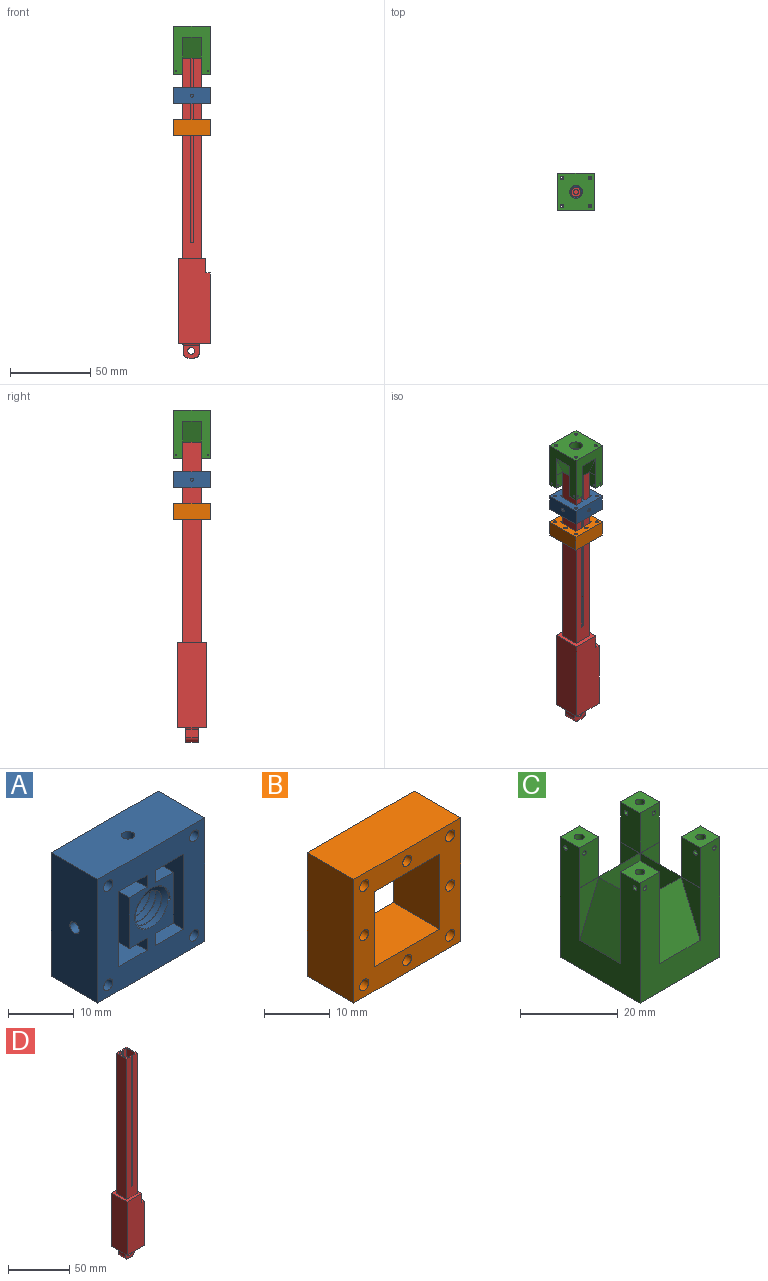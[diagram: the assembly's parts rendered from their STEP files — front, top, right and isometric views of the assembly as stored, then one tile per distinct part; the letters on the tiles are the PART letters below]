
ASSEMBLY  parts=4 mates=7
PART A: 42 faces, bbox 23.6x11.5x23.6 mm
  f0: cylinder r=1mm len=10mm, axis (0,-1,0), area 62.8mm2, adj f23,f24
  f1: cylinder r=1mm len=10mm, axis (0,-1,0), area 62.8mm2, adj f23,f24
  f2: cylinder r=1mm len=10mm, axis (0,-1,0), area 62.8mm2, adj f23,f24
  f3: cylinder r=1mm len=4mm, axis (-1,0,0), area 25.1mm2, adj f4,f32
  f4: plane 2x2mm, normal (-1,0,0), area 3.1mm2, adj f3
  f5: cylinder r=1mm len=4mm, axis (0,0,-1), area 25.1mm2, adj f6,f31
  f6: plane 2x2mm, normal (0,0,-1), area 3.1mm2, adj f5
  f7: cylinder r=1mm len=4mm, axis (1,0,0), area 25.1mm2, adj f8,f38
  f8: plane 2x2mm, normal (1,0,0), area 3.1mm2, adj f7
  f9: plane 10x2.25mm, normal (1,0,0), area 22.5mm2, adj f21,f23,f24,f35
  f10: plane 10x2.25mm, normal (-1,0,0), area 22.5mm2, adj f12,f23,f24,f29
  f11: plane 10x3.85mm, normal (0,0,-1), area 38.5mm2, adj f22,f23,f24,f28
  f12: plane 10x3.85mm, normal (0,0,1), area 38.5mm2, adj f10,f22,f23,f24
  f13: plane 0.54x0.26mm, normal (0,0,1), area 0.1mm2, adj f17,f18,f23,f26
  f14: bspline ~9.47x9.17mm, area 18.6mm2, adj f15,f18,f23,f25
  f15: bspline ~10.3x9.24mm, area 170.5mm2, adj f14,f16,f23,f25
  f16: cylinder r=3.12mm len=9.75mm, axis (0,1,0), area 16.6mm2, adj f15,f17,f23,f25
  f17: bspline ~10.51x9.25mm, area 181.5mm2, adj f13,f16,f23,f24,f25,f26
  f18: cylinder r=4.1mm len=10mm, axis (0,-1,0), area 34.7mm2, adj f13,f14,f23,f24,f25,f26
  f19: plane 10x3.85mm, normal (0,0,-1), area 38.5mm2, adj f20,f23,f24,f27
  f20: plane 10x9.5mm, normal (1,0,0), area 95mm2, adj f19,f21,f23,f24
  f21: plane 10x3.85mm, normal (0,0,1), area 38.5mm2, adj f9,f20,f23,f24
  f22: plane 10x9.5mm, normal (-1,0,0), area 95mm2, adj f11,f12,f23,f24
  f23: plane 23.59x23.59mm, normal (0,-1,0), area 376.9mm2, adj f0,f1,f2,f9,f10,f11,f12,f13
  f24: plane 23.14x23.14mm, normal (0,1,0), area 367.6mm2, adj f0,f1,f2,f9,f10,f11,f12,f17
  f25: plane 0.98x0.88mm, normal (0,0,-1), area 0.6mm2, adj f14,f15,f16,f17,f18,f24
  f26: bspline ~9.79x9.47mm, area 18.6mm2, adj f13,f17,f18,f24
  f27: plane 10x2.25mm, normal (1,0,0), area 22.5mm2, adj f19,f23,f24,f30
  f28: plane 10x2.25mm, normal (-1,0,0), area 22.5mm2, adj f11,f23,f24,f37
  f29: plane 10x6.1mm, normal (0,0,-1), area 61mm2, adj f10,f23,f24,f36
  f30: plane 10x6.1mm, normal (0,0,1), area 61mm2, adj f23,f24,f27,f34
  f31: plane 23x10mm, normal (0,0,-1), area 226.9mm2, adj f5,f23,f24,f32,f38
  f32: plane 23x10mm, normal (-1,0,0), area 226.9mm2, adj f3,f23,f24,f31,f33
  f33: plane 23x10mm, normal (0,0,1), area 226.9mm2, adj f23,f24,f32,f38,f39
  f34: plane 14x10mm, normal (-1,0,0), area 140mm2, adj f23,f24,f30,f35
  f35: plane 10x6.1mm, normal (0,0,-1), area 61mm2, adj f9,f23,f24,f34
  f36: plane 14x10mm, normal (1,0,0), area 140mm2, adj f23,f24,f29,f37
  f37: plane 10x6.1mm, normal (0,0,1), area 61mm2, adj f23,f24,f28,f36
  f38: plane 23x10mm, normal (1,0,0), area 226.9mm2, adj f7,f23,f24,f31,f33
  f39: cylinder r=1mm len=4mm, axis (0,0,1), area 25.1mm2, adj f33,f40
  f40: plane 2x2mm, normal (0,0,1), area 3.1mm2, adj f39
  f41: cylinder r=1mm len=10mm, axis (0,-1,0), area 62.8mm2, adj f23,f24
PART B: 18 faces, bbox 23x10x23 mm
  f0: cylinder r=1mm len=10mm, axis (0,-1,0), area 62.8mm2, adj f11,f12
  f1: cylinder r=1mm len=10mm, axis (0,-1,0), area 62.8mm2, adj f11,f12
  f2: cylinder r=1mm len=10mm, axis (0,-1,0), area 62.8mm2, adj f11,f12
  f3: plane 23x10mm, normal (0,0,-1), area 230mm2, adj f4,f10,f11,f12
  f4: plane 23x10mm, normal (1,0,0), area 230mm2, adj f3,f5,f11,f12
  f5: plane 23x10mm, normal (0,0,1), area 230mm2, adj f4,f10,f11,f12
  f6: plane 14x10mm, normal (-1,0,0), area 140mm2, adj f7,f9,f11,f12
  f7: plane 14x10mm, normal (0,0,1), area 140mm2, adj f6,f8,f11,f12
  f8: plane 14x10mm, normal (1,0,0), area 140mm2, adj f7,f9,f11,f12
  f9: plane 14x10mm, normal (0,0,-1), area 140mm2, adj f6,f8,f11,f12
  f10: plane 23x10mm, normal (-1,0,0), area 230mm2, adj f3,f5,f11,f12
  f11: plane 23x23mm, normal (0,-1,0), area 309.1mm2, adj f0,f1,f2,f3,f4,f5,f6,f7
  f12: plane 23x23mm, normal (0,1,0), area 309.1mm2, adj f0,f1,f2,f3,f4,f5,f6,f7
  f13: cylinder r=0.95mm len=10mm, axis (0,-1,0), area 59.7mm2, adj f11,f12
  f14: cylinder r=0.95mm len=10mm, axis (0,-1,0), area 59.7mm2, adj f11,f12
  f15: cylinder r=0.95mm len=10mm, axis (0,-1,0), area 59.7mm2, adj f11,f12
  f16: cylinder r=0.95mm len=10mm, axis (0,-1,0), area 59.7mm2, adj f11,f12
  f17: cylinder r=1mm len=10mm, axis (0,-1,0), area 62.8mm2, adj f11,f12
PART C: 63 faces, bbox 23x23x30 mm
  f0: cylinder r=4mm len=8mm, axis (0,0,-1), area 125.7mm2, adj f17,f22
  f1: cylinder r=0.5mm len=1.5mm, axis (1,0,0), area 3.7mm2, adj f13,f60,f61
  f2: plane 5.5x0.1mm, normal (0,0,1), area 0.6mm2, adj f15,f18,f54,f56
  f3: plane 5.5x0.1mm, normal (0,0,1), area 0.5mm2, adj f13,f19,f25,f57
  f4: cylinder r=0.5mm len=1.5mm, axis (0,-1,0), area 3.7mm2, adj f15,f50,f51
  f5: plane 5.5x0.1mm, normal (0,0,1), area 0.6mm2, adj f16,f21,f44,f46
  f6: plane 5.5x0.1mm, normal (0,0,1), area 0.6mm2, adj f15,f18,f47,f55
  f7: cylinder r=0.5mm len=1.5mm, axis (-1,0,0), area 3.7mm2, adj f16,f40,f41
  f8: plane 5.5x0.1mm, normal (0,0,1), area 0.6mm2, adj f10,f20,f34,f36
  f9: plane 5.5x0.1mm, normal (0,0,1), area 0.6mm2, adj f16,f21,f37,f45
  f10: plane 30x23mm, normal (0,1,0), area 415mm2, adj f8,f11,f13,f14,f16,f17,f27,f28
  f11: cylinder r=0.5mm len=1.5mm, axis (0,1,0), area 3.7mm2, adj f10,f30,f31
  f12: plane 5.5x0.1mm, normal (0,0,1), area 0.6mm2, adj f13,f19,f24,f26
  f13: plane 30x23mm, normal (1,0,0), area 415mm2, adj f1,f3,f10,f12,f15,f17,f23,f24
  f14: plane 5.5x0.1mm, normal (0,0,1), area 0.6mm2, adj f10,f20,f27,f35
  f15: plane 30x23mm, normal (0,-1,0), area 415mm2, adj f2,f4,f6,f13,f16,f17,f47,f48
  f16: plane 30x23mm, normal (-1,0,0), area 415mm2, adj f5,f7,f9,f10,f15,f17,f37,f38
  f17: plane 23x23mm, normal (0,0,-1), area 466.2mm2, adj f0,f10,f13,f15,f16,f32,f42,f52
  f18: plane 15x12mm, normal (0,1,0), area 180mm2, adj f2,f6,f19,f21,f22,f53
  f19: plane 15x12mm, normal (-1,0,0), area 180mm2, adj f3,f12,f18,f20,f22,f23
  f20: plane 15x12mm, normal (0,-1,0), area 180mm2, adj f8,f14,f19,f21,f22,f33
  f21: plane 15x12mm, normal (1,0,0), area 180mm2, adj f5,f9,f18,f20,f22,f43
  f22: plane 12x12mm, normal (0,0,1), area 93.7mm2, adj f0,f18,f19,f20,f21
  f23: plane 13x11.8mm, normal (0.92,0,0.39), area 166.6mm2, adj f13,f19,f24,f25
  f24: plane 13x5.5mm, normal (0,-1,0), area 35.8mm2, adj f12,f13,f23
  f25: plane 13x5.5mm, normal (0,1,0), area 35.8mm2, adj f3,f13,f23
  f26: plane 10x5.5mm, normal (0,-1,0), area 54.2mm2, adj f12,f13,f27,f28,f29
  f27: plane 10x5.5mm, normal (-1,0,0), area 54.2mm2, adj f10,f14,f26,f28,f31
  f28: plane 5.5x5.5mm, normal (0,0,1), area 27.1mm2, adj f10,f13,f26,f27,f32
  f29: cylinder r=0.5mm len=4mm, axis (0,1,0), area 10.5mm2, adj f26,f30,f31,f32
  f30: cylinder r=0.5mm len=1.5mm, axis (1,0,0), area 3.7mm2, adj f11,f13,f29
  f31: cylinder r=0.5mm len=4mm, axis (1,0,0), area 10.5mm2, adj f11,f27,f29,f32
  f32: cylinder r=1mm len=30mm, axis (0,0,1), area 186.5mm2, adj f17,f28,f29,f31
  f33: plane 13x11.8mm, normal (0,0.92,0.39), area 166.6mm2, adj f10,f20,f34,f35
  f34: plane 13x5.5mm, normal (1,0,0), area 35.8mm2, adj f8,f10,f33
  f35: plane 13x5.5mm, normal (-1,0,0), area 35.8mm2, adj f10,f14,f33
  f36: plane 10x5.5mm, normal (1,0,0), area 54.2mm2, adj f8,f10,f37,f38,f39
  f37: plane 10x5.5mm, normal (0,-1,0), area 54.2mm2, adj f9,f16,f36,f38,f41
  f38: plane 5.5x5.5mm, normal (0,0,1), area 27.1mm2, adj f10,f16,f36,f37,f42
  f39: cylinder r=0.5mm len=4mm, axis (-1,0,0), area 10.5mm2, adj f36,f40,f41,f42
  f40: cylinder r=0.5mm len=1.5mm, axis (0,1,0), area 3.7mm2, adj f7,f10,f39
  f41: cylinder r=0.5mm len=4mm, axis (0,1,0), area 10.5mm2, adj f7,f37,f39,f42
  f42: cylinder r=1mm len=30mm, axis (0,0,1), area 186.5mm2, adj f17,f38,f39,f41
  f43: plane 13x11.8mm, normal (-0.92,0,0.39), area 166.6mm2, adj f16,f21,f44,f45
  f44: plane 13x5.5mm, normal (0,1,0), area 35.8mm2, adj f5,f16,f43
  f45: plane 13x5.5mm, normal (0,-1,0), area 35.8mm2, adj f9,f16,f43
  f46: plane 10x5.5mm, normal (0,1,0), area 54.2mm2, adj f5,f16,f47,f48,f49
  f47: plane 10x5.5mm, normal (1,0,0), area 54.2mm2, adj f6,f15,f46,f48,f51
  f48: plane 5.5x5.5mm, normal (0,0,1), area 27.1mm2, adj f15,f16,f46,f47,f52
  f49: cylinder r=0.5mm len=4mm, axis (0,-1,0), area 10.5mm2, adj f46,f50,f51,f52
  f50: cylinder r=0.5mm len=1.5mm, axis (-1,0,0), area 3.7mm2, adj f4,f16,f49
  f51: cylinder r=0.5mm len=4mm, axis (-1,0,0), area 10.5mm2, adj f4,f47,f49,f52
  f52: cylinder r=1mm len=30mm, axis (0,0,1), area 186.5mm2, adj f17,f48,f49,f51
  f53: plane 13x11.8mm, normal (0,-0.92,0.39), area 166.6mm2, adj f15,f18,f54,f55
  f54: plane 13x5.5mm, normal (-1,0,0), area 35.8mm2, adj f2,f15,f53
  f55: plane 13x5.5mm, normal (1,0,0), area 35.8mm2, adj f6,f15,f53
  f56: plane 10x5.5mm, normal (-1,0,0), area 54.2mm2, adj f2,f15,f57,f58,f59
  f57: plane 10x5.5mm, normal (0,1,0), area 54.2mm2, adj f3,f13,f56,f58,f61
  f58: plane 5.5x5.5mm, normal (0,0,1), area 27.1mm2, adj f13,f15,f56,f57,f62
  f59: cylinder r=0.5mm len=4mm, axis (1,0,0), area 10.5mm2, adj f56,f60,f61,f62
  f60: cylinder r=0.5mm len=1.5mm, axis (0,-1,0), area 3.7mm2, adj f1,f15,f59
  f61: cylinder r=0.5mm len=4mm, axis (0,-1,0), area 10.5mm2, adj f1,f57,f59,f62
  f62: cylinder r=1mm len=30mm, axis (0,0,1), area 186.5mm2, adj f17,f58,f59,f61
PART D: 39 faces, bbox 20x18x202 mm
  f0: plane 140x12mm, normal (0,-1,0), area 1420mm2, adj f1,f3,f13,f14,f17,f34,f35,f36
  f1: plane 12x5mm, normal (0,0,1), area 20mm2, adj f0,f10,f12,f14,f15,f16,f31,f36
  f2: plane 20x18mm, normal (0,0,-1), area 240mm2, adj f4,f7,f8,f9,f27,f28,f29,f30
  f3: plane 18x17mm, normal (0,0,1), area 162mm2, adj f0,f6,f7,f8,f9,f13,f14,f15
  f4: plane 44x18mm, normal (1,0,0), area 792mm2, adj f2,f5,f8,f9
  f5: plane 18x3mm, normal (0,0,1), area 54mm2, adj f4,f6,f8,f9
  f6: plane 18x9mm, normal (1,0,0), area 162mm2, adj f3,f5,f8,f9
  f7: plane 53x18mm, normal (-1,0,0), area 954mm2, adj f2,f3,f8,f9
  f8: plane 53x20mm, normal (0,-1,0), area 1033mm2, adj f2,f3,f4,f5,f6,f7
  f9: plane 53x20mm, normal (0,1,0), area 1033mm2, adj f2,f3,f4,f5,f6,f7
  f10: plane 140x10mm, normal (0,1,0), area 1140mm2, adj f1,f11,f16,f17,f18,f34,f35,f36
  f11: plane 140x10mm, normal (1,0,0), area 1400mm2, adj f10,f12,f17,f18
  f12: plane 140x10mm, normal (0,-1,0), area 1140mm2, adj f1,f11,f16,f17,f18,f31,f32,f33
  f13: plane 140x12mm, normal (-1,0,0), area 1680mm2, adj f0,f3,f15,f17
  f14: plane 140x12mm, normal (1,0,0), area 1680mm2, adj f0,f1,f3,f15
  f15: plane 140x12mm, normal (0,1,0), area 1420mm2, adj f1,f3,f13,f14,f17,f31,f32,f33
  f16: plane 140x10mm, normal (-1,0,0), area 1400mm2, adj f1,f10,f12,f18
  f17: plane 12x5mm, normal (0,0,1), area 20mm2, adj f0,f10,f11,f12,f13,f15,f33,f34
  f18: plane 10x10mm, normal (0,0,1), area 92.9mm2, adj f10,f11,f12,f16,f37
  f19: plane 8x5mm, normal (-1,0,0), area 40mm2, adj f20,f22,f26,f27
  f20: plane 10x8mm, normal (0,1,0), area 62mm2, adj f19,f21,f23,f24,f25,f26,f28
  f21: plane 8x5mm, normal (1,0,0), area 40mm2, adj f20,f22,f25,f30
  f22: plane 10x8mm, normal (0,-1,0), area 62mm2, adj f19,f21,f23,f24,f25,f26,f29
  f23: plane 8x4mm, normal (0,0,-1), area 32mm2, adj f20,f22,f25,f26
  f24: cylinder r=2.12mm len=8mm, axis (0,-1,0), area 106.8mm2, adj f20,f22
  f25: cylinder r=3mm len=8mm, axis (0,1,0), area 37.7mm2, adj f20,f21,f22,f23
  f26: cylinder r=3mm len=8mm, axis (0,-1,0), area 37.7mm2, adj f19,f20,f22,f23
  f27: cylinder r=1mm len=10mm, axis (0,1,0), area 13.7mm2, adj f2,f19,f28,f29
  f28: cylinder r=1mm len=12mm, axis (1,0,0), area 16.8mm2, adj f2,f20,f27,f30
  f29: cylinder r=1mm len=12mm, axis (-1,0,0), area 16.8mm2, adj f2,f22,f27,f30
  f30: cylinder r=1mm len=10mm, axis (0,-1,0), area 13.7mm2, adj f2,f21,f28,f29
  f31: plane 130x1mm, normal (-1,0,0), area 130mm2, adj f1,f12,f15,f32
  f32: plane 2x1mm, normal (0,0,1), area 2mm2, adj f12,f15,f31,f33
  f33: plane 130x1mm, normal (1,0,0), area 130mm2, adj f12,f15,f17,f32
  f34: plane 130x1mm, normal (1,0,0), area 130mm2, adj f0,f10,f17,f35
  f35: plane 2x1mm, normal (0,0,1), area 2mm2, adj f0,f10,f34,f36
  f36: plane 130x1mm, normal (-1,0,0), area 130mm2, adj f0,f1,f10,f35
  f37: cylinder r=1.5mm len=135mm, axis (0,0,-1), area 1272.3mm2, adj f18,f38
  f38: plane 3x3mm, normal (0,0,1), area 7.1mm2, adj f37
PLACE A rot(axis=(-1,0,0),90deg) t=(-3.72,-6.38,147.75)mm
PLACE B rot(axis=(0.58,0.58,0.58),120deg) t=(-3.72,-6.38,137.94)mm
PLACE C rot(axis=(1,0,0),180deg) t=(-3.72,-6.38,196.19)mm
PLACE D t=(-2.22,2.62,20.19)mm fixed
MATE planar A.f39 <-> B.f4  axis (0,1,0) through (-3.72,5.12,152.75)mm
MATE planar D.f0 <-> C.f20  axis (0,-1,0) through (-3.72,-12.38,120.28)mm
MATE planar C.f21 <-> D.f13  axis (1,0,0) through (-9.72,-6.38,183.69)mm
MATE planar D.f17 <-> C.f0  axis (0,0,1) through (-7.22,-0.38,191.19)mm
MATE slider A.f16 <-> D.f37  axis (0,0,-1) through (-3.72,-6.38,152.84)mm
MATE parallel D.f14 <-> A.f3  axis (1,0,0) through (2.28,-6.38,121.19)mm
MATE planar A.f7 <-> B.f5  axis (1,0,0) through (7.78,-6.38,152.75)mm
